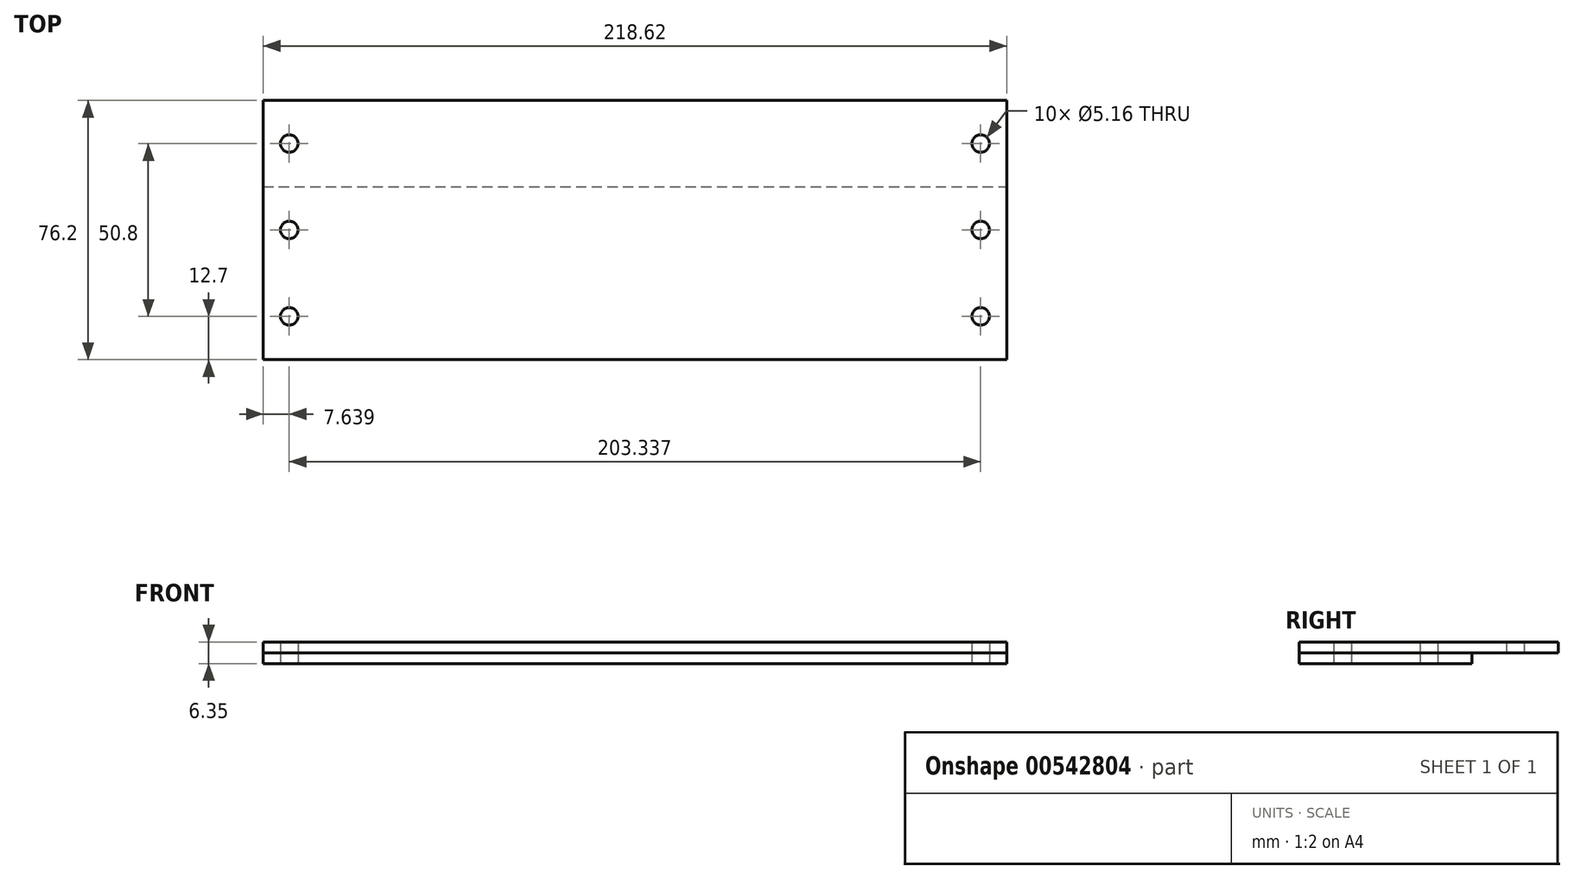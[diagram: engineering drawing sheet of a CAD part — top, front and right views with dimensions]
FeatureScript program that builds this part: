
annotation { "Feature Type Name" : "Feature", "Feature Type Description" : "" }
export const myFeature = defineFeature(function(context is Context, id is Id, definition is map)
    precondition{}
    {
        {
            var Q0;
            Q0=qCreatedBy(makeId("Top.planeOp"),FACE);
            var sketch = newSketch(context, id + "F0", { "sketchPlane" : qUnion([Q0])});
            skLineSegment(sketch, "E0.bottom", {"start": v(-114.65, 38.1) * mm, "end": v(103.97, 38.1) * mm});
            skLineSegment(sketch, "E0.top", {"start": v(-114.65, -38.1) * mm, "end": v(103.97, -38.1) * mm});
            skLineSegment(sketch, "E0.left", {"start": v(-114.65, 38.1) * mm, "end": v(-114.65, -38.1) * mm});
            skLineSegment(sketch, "E0.right", {"start": v(103.97, 38.1) * mm, "end": v(103.97, -38.1) * mm});
            skLineSegment(sketch, "E1", {"start": v(-114.65, 12.7) * mm, "end": v(103.97, 12.7) * mm});
            skCircle(sketch, "E2", {"center": v(-107.01, -25.4) * mm, "radius": 2.58 * mm});
            skCircle(sketch, "E3", {"center": v(-107.01, 0) * mm, "radius": 2.58 * mm});
            skCircle(sketch, "E4", {"center": v(-107.01, 25.4) * mm, "radius": 2.58 * mm});
            skCircle(sketch, "E5", {"center": v(96.33, 25.4) * mm, "radius": 2.58 * mm});
            skCircle(sketch, "E6", {"center": v(96.33, 0) * mm, "radius": 2.58 * mm});
            skCircle(sketch, "E7", {"center": v(96.33, -25.4) * mm, "radius": 2.58 * mm});
            skLineSegment(sketch, "E8", {"start": v(-107.01, 0) * mm, "end": v(-107.01, -25.4) * mm, "construction": true});
            skLineSegment(sketch, "E9", {"start": v(-107.01, 0) * mm, "end": v(-107.01, 25.4) * mm, "construction": true});
            skLineSegment(sketch, "E10", {"start": v(96.33, 25.4) * mm, "end": v(96.33, 0) * mm, "construction": true});
            skLineSegment(sketch, "E11", {"start": v(96.33, 0) * mm, "end": v(96.33, -25.4) * mm, "construction": true});
            skSolve(sketch);
        }
        {
            var Q0;
            {var subQ1=sQuery(id+"F0.wireOp",EDGE,"E0.top");Q0=makeQuery(id+"F0.imprint","IMPRINT",FACE,{"disambiguationData":[TD([[makeQuery(id+"F0.imprint","IMPRINT",EDGE,{"derivedFrom":subQ1}),1.0]])]});}
            extrude(context, id + "F1", {"entities" : qUnion([Q0]), "depth" : 3.17 * mm});
        }
        {
            var Q0;
            {var subQ1=sQuery(id+"F0.wireOp",EDGE,"E0.top");Q0=makeQuery(id+"F0.imprint","IMPRINT",FACE,{"disambiguationData":[TD([[makeQuery(id+"F0.imprint","IMPRINT",EDGE,{"derivedFrom":subQ1}),1.0]])]});}
            var Q1;
            {var subQ2=sQuery(id+"F0.wireOp",EDGE,"E0.bottom");Q1=makeQuery(id+"F0.imprint","IMPRINT",FACE,{"disambiguationData":[TD([[makeQuery(id+"F0.imprint","IMPRINT",EDGE,{"derivedFrom":subQ2}),-1.0]])]});}
            extrude(context, id + "F2", {"entities" : qUnion([Q0, Q1]), "depth" : 6.35 * mm, "hasSecondDirection" : true, "secondDirectionOppositeDirection" : true, "secondDirectionDepth" : -3.17 * mm});
        }
    });
